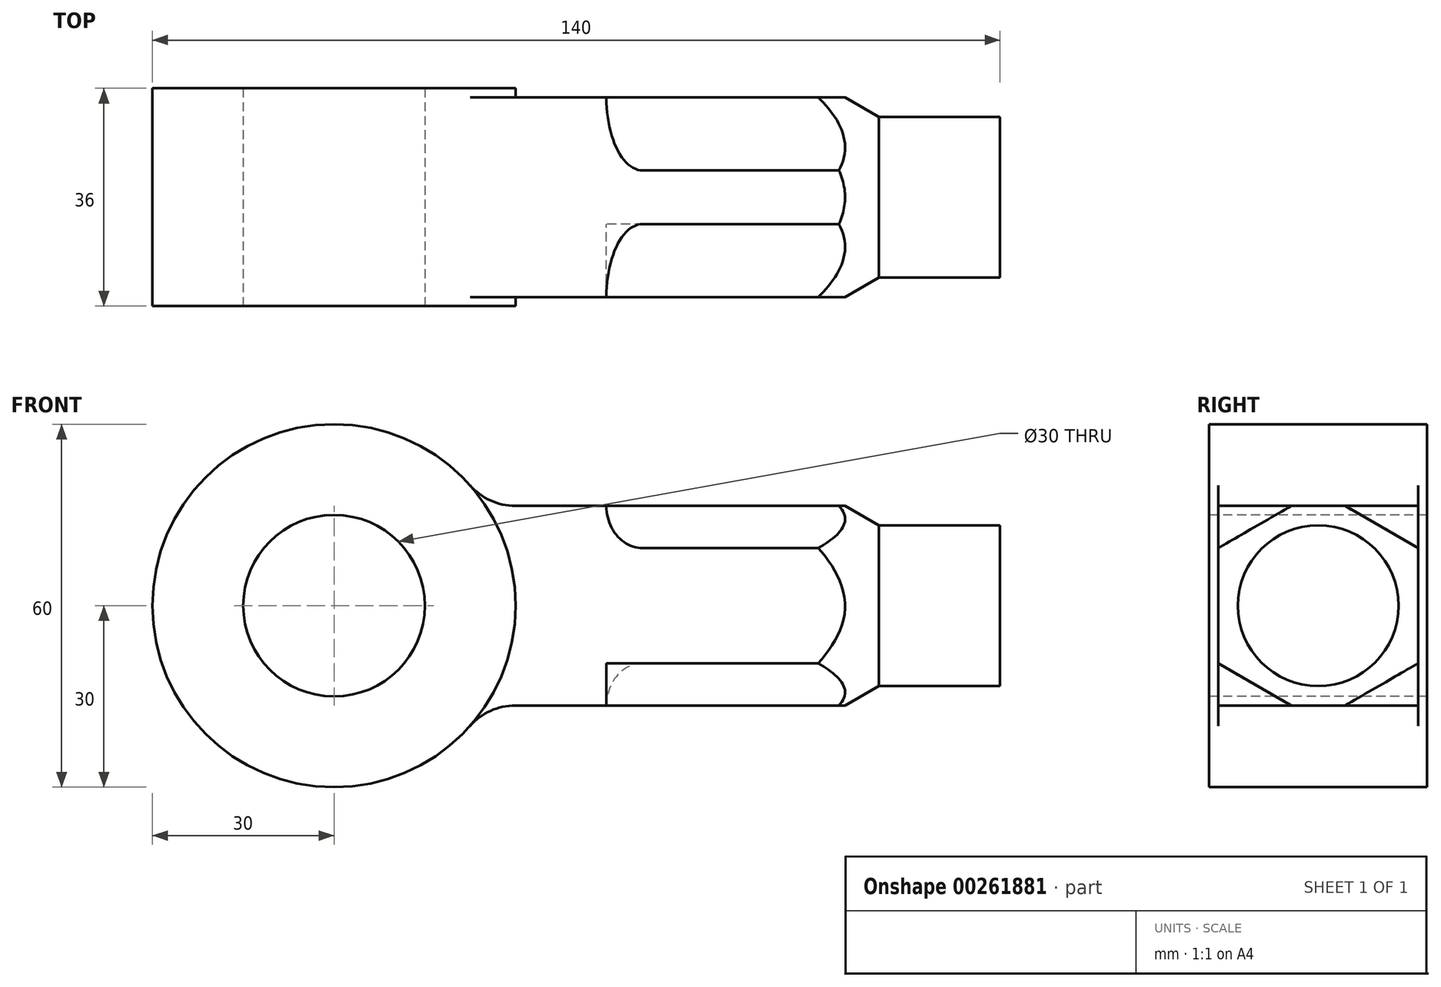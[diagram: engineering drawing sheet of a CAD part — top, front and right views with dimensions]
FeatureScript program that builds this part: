
annotation { "Feature Type Name" : "Feature", "Feature Type Description" : "" }
export const myFeature = defineFeature(function(context is Context, id is Id, definition is map)
    precondition{}
    {
        {
            var Q0;
            Q0=qCreatedBy(makeId("Front.planeOp"),FACE);
            var sketch = newSketch(context, id + "F0", { "sketchPlane" : qUnion([Q0])});
            skCircle(sketch, "E0", {"center": v(0, 0) * mm, "radius": 30 * mm});
            skCircle(sketch, "E1", {"center": v(0, 0) * mm, "radius": 15 * mm});
            skSolve(sketch);
        }
        {
            var Q0;
            Q0 = qSketchRegion(id + "F0", true);
            extrude(context, id + "F1", {"entities" : qUnion([Q0]), "endBound" : BoundingType.SYMMETRIC, "oppositeDirection" : true, "depth" : 36 * mm});
        }
        {
            var Q0;
            Q0=qCreatedBy(makeId("Front.planeOp"),FACE);
            var sketch = newSketch(context, id + "F2", { "sketchPlane" : qUnion([Q0])});
            skLineSegment(sketch, "E2", {"start": v(25, 16.5) * mm, "end": v(45, 16.5) * mm});
            skLineSegment(sketch, "E3", {"start": v(45, 16.5) * mm, "end": v(45, -16.5) * mm});
            skLineSegment(sketch, "E4", {"start": v(45, -16.5) * mm, "end": v(25, -16.5) * mm});
            skLineSegment(sketch, "E5", {"start": v(25, 16.5) * mm, "end": v(25, -16.5) * mm});
            skSolve(sketch);
        }
        {
            var Q0;
            Q0 = qSketchRegion(id + "F2", true);
            extrude(context, id + "F3", {"entities" : qUnion([Q0]), "operationType" : NewBodyOperationType.ADD, "endBound" : BoundingType.SYMMETRIC, "depth" : 33 * mm});
        }
        {
            var Q0;
            Q0=makeQuery(id+"F3.opExtrude","SWEPT_FACE",FACE,{"disambiguationData":[OSD([sQuery(id+"F2.wireOp",EDGE,"E3")])]});
            var sketch = newSketch(context, id + "F4", { "sketchPlane" : qUnion([Q0])});
            skCircle(sketch, "E6.cCircle", {"center": v(0, 0) * mm, "radius": 16.5 * mm, "construction": true});
            skLineSegment(sketch, "E6.0", {"start": v(-16.5, -9.53) * mm, "end": v(-16.5, 9.53) * mm});
            skLineSegment(sketch, "E6.1", {"start": v(-16.5, 9.53) * mm, "end": v(0, 19.05) * mm});
            skLineSegment(sketch, "E6.2", {"start": v(0, 19.05) * mm, "end": v(16.5, 9.53) * mm});
            skLineSegment(sketch, "E6.3", {"start": v(16.5, 9.53) * mm, "end": v(16.5, -9.53) * mm});
            skLineSegment(sketch, "E6.4", {"start": v(16.5, -9.53) * mm, "end": v(0, -19.05) * mm});
            skLineSegment(sketch, "E6.5", {"start": v(0, -19.05) * mm, "end": v(-16.5, -9.53) * mm});
            skPoint(sketch, "E6.0.midPoint", {"position": v(-16.5, 0) * mm});
            skSolve(sketch);
        }
        {
            var Q0;
            Q0 = qSketchRegion(id + "F4", true);
            extrude(context, id + "F5", {"entities" : qUnion([Q0]), "operationType" : NewBodyOperationType.ADD, "depth" : 45 * mm});
        }
        {
            var Q0;
            Q0=makeQuery(id+"F5.boolean.opBoolean","MERGE",FACE,{"derivedFrom":[makeQuery(id+"F3.opExtrude","CAP_FACE",FACE,{"disambiguationData":[OSD([sQuery(id+"F2.wireOp",EDGE,"E2"),sQuery(id+"F2.wireOp",EDGE,"E3"),sQuery(id+"F2.wireOp",EDGE,"E4"),sQuery(id+"F2.wireOp",EDGE,"E5")])],"isStart":true}),makeQuery(id+"F5.opExtrude","SWEPT_FACE",FACE,{"disambiguationData":[OSD([sQuery(id+"F4.wireOp",EDGE,"E6.3")])]})]});
            var Q1;
            Q1=makeQuery(id+"F5.boolean.opBoolean","MERGE",FACE,{"derivedFrom":[makeQuery(id+"F3.opExtrude","CAP_FACE",FACE,{"disambiguationData":[OSD([sQuery(id+"F2.wireOp",EDGE,"E2"),sQuery(id+"F2.wireOp",EDGE,"E3"),sQuery(id+"F2.wireOp",EDGE,"E4"),sQuery(id+"F2.wireOp",EDGE,"E5")])],"isStart":false}),makeQuery(id+"F5.opExtrude","SWEPT_FACE",FACE,{"disambiguationData":[OSD([sQuery(id+"F4.wireOp",EDGE,"E6.0")])]})]});
            cPlane(context, id + "F6", {"entities" : qUnion([Q0, Q1]), "cplaneType" : CPlaneType.MID_PLANE, "offset" : 25 * mm, "width" : 150 * mm, "height" : 150 * mm});
        }
        {
            var Q0;
            Q0=qCreatedBy(id+"F6.planeOp",FACE);
            var sketch = newSketch(context, id + "F7", { "sketchPlane" : qUnion([Q0])});
            skLineSegment(sketch, "E7", {"start": v(-90, 13.28) * mm, "end": v(-90, 19.05) * mm});
            skLineSegment(sketch, "E8", {"start": v(-90, 19.05) * mm, "end": v(-80, 19.05) * mm});
            skLineSegment(sketch, "E9", {"start": v(-80, 19.05) * mm, "end": v(-90, 13.28) * mm});
            skLineSegment(sketch, "E10", {"start": v(-53.89, 0) * mm, "end": v(-99.66, 0) * mm, "construction": true});
            skSolve(sketch);
        }
        {
            var Q0;
            Q0 = qSketchRegion(id + "F7", true);
            var Q1;
            Q1=sQuery(id+"F7.wireOp",EDGE,"E10");
            revolve(context, id + "F8", {"operationType" : NewBodyOperationType.REMOVE, "entities" : qUnion([Q0]), "axis" : qUnion([Q1]), "revolveType" : RevolveType.FULL, "oppositeDirection" : true});
        }
        {
            var Q0;
            {var subQ0=sQuery(id+"F4.wireOp",EDGE,"E6.1");var subQ1=sQuery(id+"F4.wireOp",EDGE,"E6.2");Q0=makeQuery(id+"F5.boolean.opBoolean","SPLIT",FACE,{"disambiguationData":[TD([makeQuery(id+"F3.opExtrude","SWEPT_FACE",FACE,{"disambiguationData":[OSD([sQuery(id+"F2.wireOp",EDGE,"E2")])]})])],"derivedFrom":makeQuery(id+"F5.opExtrude","CAP_FACE",FACE,{"disambiguationData":[OSD([sQuery(id+"F4.wireOp",EDGE,"E6.0"),subQ0,subQ1,sQuery(id+"F4.wireOp",EDGE,"E6.3"),sQuery(id+"F4.wireOp",EDGE,"E6.4"),sQuery(id+"F4.wireOp",EDGE,"E6.5")])],"isStart":true})});}
            extrude(context, id + "F9", {"entities" : qUnion([Q0]), "operationType" : NewBodyOperationType.REMOVE, "endBound" : BoundingType.THROUGH_ALL, "oppositeDirection" : true, "depth" : 25 * mm});
        }
        {
            var Q0;
            {var subQ0=sQuery(id+"F4.wireOp",EDGE,"E6.4");var subQ1=sQuery(id+"F4.wireOp",EDGE,"E6.5");Q0=makeQuery(id+"F5.boolean.opBoolean","SPLIT",FACE,{"disambiguationData":[TD([makeQuery(id+"F3.opExtrude","SWEPT_FACE",FACE,{"disambiguationData":[OSD([sQuery(id+"F2.wireOp",EDGE,"E4")])]})])],"derivedFrom":makeQuery(id+"F5.opExtrude","CAP_FACE",FACE,{"disambiguationData":[OSD([sQuery(id+"F4.wireOp",EDGE,"E6.0"),sQuery(id+"F4.wireOp",EDGE,"E6.1"),sQuery(id+"F4.wireOp",EDGE,"E6.2"),sQuery(id+"F4.wireOp",EDGE,"E6.3"),subQ0,subQ1])],"isStart":true})});}
            extrude(context, id + "F10", {"entities" : qUnion([Q0]), "operationType" : NewBodyOperationType.REMOVE, "endBound" : BoundingType.THROUGH_ALL, "oppositeDirection" : true, "depth" : 25 * mm});
        }
        {
            var Q0;
            {var subQ0=sQuery(id+"F4.wireOp",EDGE,"E6.0");var subQ2=sQuery(id+"F4.wireOp",EDGE,"E6.5");Q0=makeQuery(id+"F5.boolean.opBoolean","SPLIT",EDGE,{"disambiguationData":[TD([makeQuery(id+"F5.opExtrude","SWEPT_FACE",FACE,{"disambiguationData":[OSD([subQ0])]})])],"derivedFrom":makeQuery(id+"F5.opExtrude","CAP_EDGE",EDGE,{"disambiguationData":[OSD([subQ2])],"isStart":true})});}
            var Q1;
            {var subQ0=sQuery(id+"F4.wireOp",EDGE,"E6.0");var subQ3=sQuery(id+"F4.wireOp",EDGE,"E6.1");Q1=makeQuery(id+"F5.boolean.opBoolean","SPLIT",EDGE,{"disambiguationData":[TD([makeQuery(id+"F5.opExtrude","SWEPT_FACE",FACE,{"disambiguationData":[OSD([subQ0])]})])],"derivedFrom":makeQuery(id+"F5.opExtrude","CAP_EDGE",EDGE,{"disambiguationData":[OSD([subQ3])],"isStart":true})});}
            var Q2;
            {var subQ0=sQuery(id+"F4.wireOp",EDGE,"E6.3");var subQ1=sQuery(id+"F4.wireOp",EDGE,"E6.2");Q2=makeQuery(id+"F5.boolean.opBoolean","SPLIT",EDGE,{"disambiguationData":[TD([makeQuery(id+"F5.opExtrude","SWEPT_FACE",FACE,{"disambiguationData":[OSD([subQ0])]})])],"derivedFrom":makeQuery(id+"F5.opExtrude","CAP_EDGE",EDGE,{"disambiguationData":[OSD([subQ1])],"isStart":true})});}
            var Q3;
            {var subQ0=sQuery(id+"F4.wireOp",EDGE,"E6.4");var subQ1=sQuery(id+"F4.wireOp",EDGE,"E6.3");Q3=makeQuery(id+"F5.boolean.opBoolean","SPLIT",EDGE,{"disambiguationData":[TD([makeQuery(id+"F5.opExtrude","SWEPT_FACE",FACE,{"disambiguationData":[OSD([subQ1])]})])],"derivedFrom":makeQuery(id+"F5.opExtrude","CAP_EDGE",EDGE,{"disambiguationData":[OSD([subQ0])],"isStart":true})});}
            fillet(context, id + "F11", {"entities" : qUnion([Q0, Q1, Q2, Q3]), "radius" : 6 * mm, "tangentPropagation" : true, "allowEdgeOverflow" : false});
        }
        {
            var Q0;
            Q0=makeQuery(id+"F5.opExtrude","CAP_FACE",FACE,{"disambiguationData":[OSD([sQuery(id+"F4.wireOp",EDGE,"E6.0"),sQuery(id+"F4.wireOp",EDGE,"E6.1"),sQuery(id+"F4.wireOp",EDGE,"E6.2"),sQuery(id+"F4.wireOp",EDGE,"E6.3"),sQuery(id+"F4.wireOp",EDGE,"E6.4"),sQuery(id+"F4.wireOp",EDGE,"E6.5")])],"isStart":false});
            var sketch = newSketch(context, id + "F12", { "sketchPlane" : qUnion([Q0])});
            skCircle(sketch, "E11.0", {"center": v(0, 0) * mm, "radius": 13.28 * mm});
            skSolve(sketch);
        }
        {
            var Q0;
            Q0 = qSketchRegion(id + "F12", true);
            extrude(context, id + "F13", {"entities" : qUnion([Q0]), "operationType" : NewBodyOperationType.ADD, "depth" : 20 * mm});
        }
        {
            var Q0;
            Q0=makeQuery(id+"F3.boolean.opBoolean","INTERSECT",EDGE,{"derivedFrom":[makeQuery(id+"F1.opExtrude","SWEPT_FACE",FACE,{"disambiguationData":[OSD([sQuery(id+"F0.wireOp",EDGE,"E0")])]}),makeQuery(id+"F3.opExtrude","SWEPT_FACE",FACE,{"disambiguationData":[OSD([sQuery(id+"F2.wireOp",EDGE,"E2")])]})]});
            var Q1;
            Q1=makeQuery(id+"F3.boolean.opBoolean","INTERSECT",EDGE,{"derivedFrom":[makeQuery(id+"F1.opExtrude","SWEPT_FACE",FACE,{"disambiguationData":[OSD([sQuery(id+"F0.wireOp",EDGE,"E0")])]}),makeQuery(id+"F3.opExtrude","SWEPT_FACE",FACE,{"disambiguationData":[OSD([sQuery(id+"F2.wireOp",EDGE,"E4")])]})]});
            fillet(context, id + "F14", {"entities" : qUnion([Q0, Q1]), "radius" : 10 * mm, "tangentPropagation" : true, "allowEdgeOverflow" : false});
        }
    });
